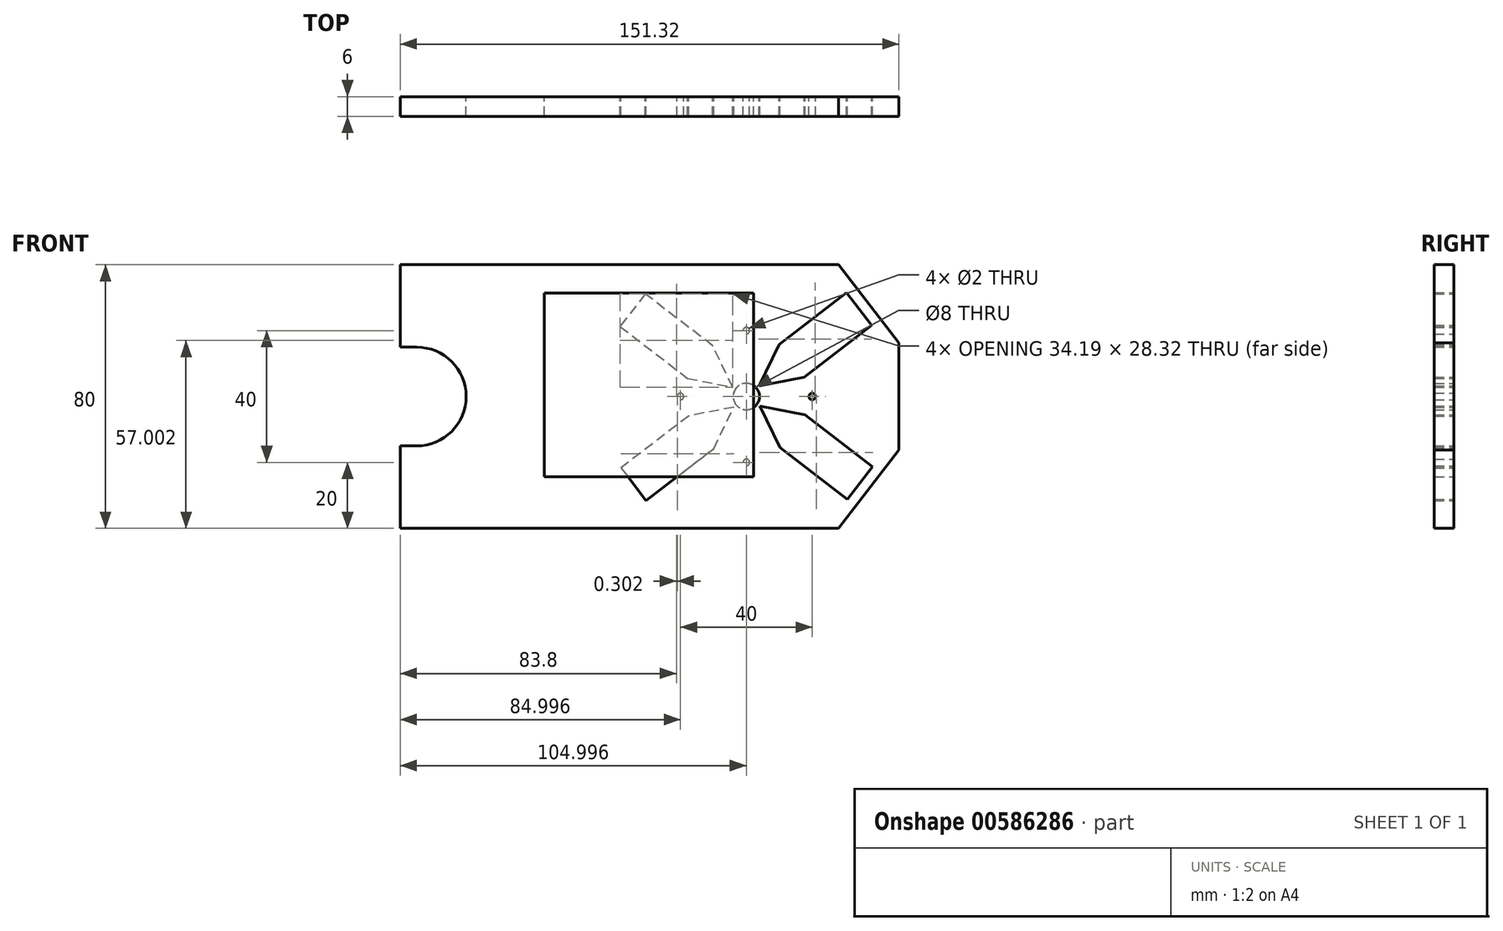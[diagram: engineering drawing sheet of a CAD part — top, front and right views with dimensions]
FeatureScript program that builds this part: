
annotation { "Feature Type Name" : "Feature", "Feature Type Description" : "" }
export const myFeature = defineFeature(function(context is Context, id is Id, definition is map)
    precondition{}
    {
        {
            var Q0;
            Q0=qCreatedBy(makeId("Front.planeOp"),FACE);
            var sketch = newSketch(context, id + "F0", { "sketchPlane" : qUnion([Q0])});
            skArc(sketch, "E0", {"start": v(33.34, 0) * mm, "mid": v(32.16, 2.83) * mm, "end": v(29.34, 4) * mm});
            skArc(sketch, "E1", {"start": v(29.34, 4) * mm, "mid": v(26.5, 2.83) * mm, "end": v(25.34, 0) * mm});
            skArc(sketch, "E2", {"start": v(25.34, 0) * mm, "mid": v(26.5, -2.83) * mm, "end": v(29.34, -4) * mm});
            skArc(sketch, "E3", {"start": v(29.34, -4) * mm, "mid": v(32.16, -2.83) * mm, "end": v(33.34, 0) * mm});
            skLineSegment(sketch, "E4", {"start": v(-8.66, -21.65) * mm, "end": v(-1.03, -31.56) * mm});
            skLineSegment(sketch, "E5", {"start": v(-1.03, -31.56) * mm, "end": v(19.44, -15.8) * mm});
            skLineSegment(sketch, "E6", {"start": v(19.44, -15.8) * mm, "end": v(25.54, -3.23) * mm});
            skLineSegment(sketch, "E7", {"start": v(25.54, -3.23) * mm, "end": v(11.82, -5.9) * mm});
            skLineSegment(sketch, "E8", {"start": v(11.82, -5.9) * mm, "end": v(-8.66, -21.65) * mm});
            skArc(sketch, "E9", {"start": v(30.34, -20) * mm, "mid": v(30.04, -19.3) * mm, "end": v(29.34, -19) * mm});
            skArc(sketch, "E10", {"start": v(29.34, -19) * mm, "mid": v(28.63, -19.3) * mm, "end": v(28.34, -20) * mm});
            skArc(sketch, "E11", {"start": v(28.34, -20) * mm, "mid": v(28.63, -20.7) * mm, "end": v(29.34, -21) * mm});
            skArc(sketch, "E12", {"start": v(29.34, -21) * mm, "mid": v(30.04, -20.7) * mm, "end": v(30.34, -20) * mm});
            skArc(sketch, "E13", {"start": v(30.34, 20) * mm, "mid": v(30.04, 20.7) * mm, "end": v(29.34, 21) * mm});
            skArc(sketch, "E14", {"start": v(29.34, 21) * mm, "mid": v(28.63, 20.7) * mm, "end": v(28.34, 20) * mm});
            skArc(sketch, "E15", {"start": v(28.34, 20) * mm, "mid": v(28.63, 19.3) * mm, "end": v(29.34, 19) * mm});
            skArc(sketch, "E16", {"start": v(29.34, 19) * mm, "mid": v(30.04, 19.3) * mm, "end": v(30.34, 20) * mm});
            skArc(sketch, "E17", {"start": v(10.34, 0) * mm, "mid": v(10.04, 0.7) * mm, "end": v(9.34, 1) * mm});
            skArc(sketch, "E18", {"start": v(9.34, 1) * mm, "mid": v(8.63, 0.7) * mm, "end": v(8.34, 0) * mm});
            skArc(sketch, "E19", {"start": v(8.34, 0) * mm, "mid": v(8.63, -0.7) * mm, "end": v(9.34, -1) * mm});
            skArc(sketch, "E20", {"start": v(9.34, -1) * mm, "mid": v(10.04, -0.7) * mm, "end": v(10.34, 0) * mm});
            skArc(sketch, "E21", {"start": v(50.34, 0) * mm, "mid": v(50.04, 0.7) * mm, "end": v(49.34, 1) * mm});
            skArc(sketch, "E22", {"start": v(49.34, 1) * mm, "mid": v(48.63, 0.7) * mm, "end": v(48.34, 0) * mm});
            skArc(sketch, "E23", {"start": v(48.34, 0) * mm, "mid": v(48.63, -0.7) * mm, "end": v(49.34, -1) * mm});
            skArc(sketch, "E24", {"start": v(49.34, -1) * mm, "mid": v(50.04, -0.7) * mm, "end": v(50.34, 0) * mm});
            skLineSegment(sketch, "E25", {"start": v(25.24, 2.84) * mm, "end": v(19.14, 15.42) * mm});
            skLineSegment(sketch, "E26", {"start": v(19.14, 15.42) * mm, "end": v(-1.34, 31.16) * mm});
            skLineSegment(sketch, "E27", {"start": v(-1.34, 31.16) * mm, "end": v(-8.96, 21.26) * mm});
            skLineSegment(sketch, "E28", {"start": v(-8.96, 21.26) * mm, "end": v(11.52, 5.5) * mm});
            skLineSegment(sketch, "E29", {"start": v(11.52, 5.5) * mm, "end": v(25.24, 2.84) * mm});
            skLineSegment(sketch, "E30", {"start": v(46.85, 5.9) * mm, "end": v(67.33, 21.65) * mm});
            skLineSegment(sketch, "E31", {"start": v(67.33, 21.65) * mm, "end": v(59.7, 31.56) * mm});
            skLineSegment(sketch, "E32", {"start": v(59.7, 31.56) * mm, "end": v(39.23, 15.8) * mm});
            skLineSegment(sketch, "E33", {"start": v(39.23, 15.8) * mm, "end": v(33.13, 3.23) * mm});
            skLineSegment(sketch, "E34", {"start": v(33.13, 3.23) * mm, "end": v(46.85, 5.9) * mm});
            skLineSegment(sketch, "E35", {"start": v(67.63, -21.26) * mm, "end": v(47.15, -5.5) * mm});
            skLineSegment(sketch, "E36", {"start": v(47.15, -5.5) * mm, "end": v(33.44, -2.84) * mm});
            skLineSegment(sketch, "E37", {"start": v(33.44, -2.84) * mm, "end": v(39.53, -15.42) * mm});
            skLineSegment(sketch, "E38", {"start": v(39.53, -15.42) * mm, "end": v(60, -31.16) * mm});
            skLineSegment(sketch, "E39", {"start": v(60, -31.16) * mm, "end": v(67.63, -21.26) * mm});
            skLineSegment(sketch, "E40", {"start": v(-75.66, -40) * mm, "end": v(-75.66, -15) * mm});
            skLineSegment(sketch, "E41", {"start": v(-75.66, -15) * mm, "end": v(-70.66, -15) * mm});
            skArc(sketch, "E42", {"start": v(-70.66, -15) * mm, "mid": v(-55.66, 0) * mm, "end": v(-70.66, 15) * mm});
            skLineSegment(sketch, "E43", {"start": v(-70.66, 15) * mm, "end": v(-75.66, 15) * mm});
            skLineSegment(sketch, "E44", {"start": v(-75.66, 15) * mm, "end": v(-75.66, 40) * mm});
            skLineSegment(sketch, "E45", {"start": v(-75.66, 40) * mm, "end": v(57.34, 40) * mm});
            skLineSegment(sketch, "E46", {"start": v(57.34, 40) * mm, "end": v(75.66, 16.25) * mm});
            skLineSegment(sketch, "E47", {"start": v(75.66, 16.25) * mm, "end": v(75.66, -16.25) * mm});
            skLineSegment(sketch, "E48", {"start": v(75.66, -16.25) * mm, "end": v(57.34, -40) * mm});
            skLineSegment(sketch, "E49", {"start": v(57.34, -40) * mm, "end": v(-75.66, -40) * mm});
            skSolve(sketch);
        }
        {
            var Q0;
            Q0=makeQuery(id+"F0.imprint","IMPRINT",FACE,{"disambiguationData":[TD([[makeQuery(id+"F0.imprint","IMPRINT",EDGE,{"derivedFrom":sQuery(id+"F0.wireOp",EDGE,"E0")}),-1.0]])]});
            extrude(context, id + "F1", {"entities" : qUnion([Q0]), "depth" : 6 * mm, "offsetDistance" : 25.4 * mm});
        }
        {
            var Q0;
            Q0=qCreatedBy(makeId("Front.planeOp"),FACE);
            var sketch = newSketch(context, id + "F2", { "sketchPlane" : qUnion([Q0])});
            skLineSegment(sketch, "E50.bottom", {"start": v(31.54, 31.44) * mm, "end": v(-31.91, 31.44) * mm});
            skLineSegment(sketch, "E50.top", {"start": v(31.54, -24.35) * mm, "end": v(-31.91, -24.35) * mm});
            skLineSegment(sketch, "E50.left", {"start": v(31.54, 31.44) * mm, "end": v(31.54, -24.35) * mm});
            skLineSegment(sketch, "E50.right", {"start": v(-31.91, 31.44) * mm, "end": v(-31.91, -24.35) * mm});
            skSolve(sketch);
        }
        {
            var Q0;
            Q0=makeQuery(id+"F2.imprint","IMPRINT",FACE,{"disambiguationData":[TD([[makeQuery(id+"F2.imprint","IMPRINT",EDGE,{"derivedFrom":sQuery(id+"F2.wireOp",EDGE,"E50.bottom")}),1.0]])]});
            extrude(context, id + "F3", {"entities" : qUnion([Q0]), "depth" : 6 * mm, "offsetDistance" : 25 * mm});
        }
    });
